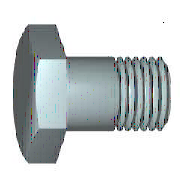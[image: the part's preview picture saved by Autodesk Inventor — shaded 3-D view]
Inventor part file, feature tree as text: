
AUTODESK INVENTOR PART (.ipt)
format: ipt  version: 2016 (Build 200138000, 138)  size: 191,488 bytes
history: native  units: mm (DEFAULTED — no unit token found)
features: sketch x3, extrude x1, chamfer x1, plane x1
ambient origin geometry x7: Origin, YZ Plane, XZ Plane, X Axis, Y Axis, Z Axis, Center Point
bodies: Solid1 (feature_tree), Body (feature_tree)
feature tree (6):
  extrude  "Head"  Depth=26.0mm
  chamfer  "Chamfer1"  Distance=5.8mm
  plane  "Work Plane1"
  sketch  "Sketch1"  dims[d0=40.0mm d1=26.0mm]
  sketch  "Sketch2"  dims[d2=10.0mm]
  sketch  "Sketch4"  dims[d12=90.0deg d3=5.8mm d4=0.0mm d5=30.0deg d21=90.0deg d6=0.920175mm d7=0.920275mm d8=0.0mm d9=0.6001mm d10=15.6mm d11=17.0mm d13=0.920275mm d14=10.0mm d15=26.0mm d16=0.0mm d19=17.0mm d55=45.0deg d57=0.0mm d58=0.0mm]
